# Revit family: FLAKE-PDI100NDFWSxx0DPO0400
name_source: partatom
category: Leuchten
units: mm (PartAtom-declared; Revit-internal decimal feet)

## family parameters
Basisbauteil = Fläche
Beim Laden mit Abzugskörper schneiden = Nein
Bemaßung runder Anschluss = Durchmesser verwenden
Gemeinsam genutzt = Nein
Lichtquelle = Ja
OmniClass-Nummer = 23.80.70.11
OmniClass-Titel = Luminaries for Internal Lighting
Raumberechnungspunkt = Nein
Teiletyp = Normal

## types (2) — shared parameters
Baugruppenkennzeichen = D5020200
Datei für fotometrisches Netz = FLAKE-PDI.IES
Emissionsform beim Rendern sichtbar = Nein
Farbfilter = 16777215
Farbtemperaturverschiebung bei Dämpfen der Lampe = <Keine Auswahl>
Hersteller = RIDI Leuchten GmbH
Lampe = LED
Modell = 0627725AH
Neigungswinkel = 90.00°
Scheinlast = 32 VA
URL = www.ridi.de
Von Breite des Rechtecks ausssenden = 993 mm  [stored 3.25787 ft]
Von Länge des Rechtecks aussenden = 133 mm  [stored 0.436352 ft]
brand = RIDI
conformity mark = CE
electrical safety class = 1
height = 42 mm  [stored 0.137795 ft]
ingress protection (IP) code = IP20
length = 1010 mm  [stored 3.31365 ft]
nominal frequency = 50-60Hz
nominal voltage = 230
rated input power = 32
voltage type (AC, DC, UC) = AC
weight = 4,2
width = 150 mm
zero-valued in all types: Vorgabe-Ansicht

## type names (no varying parameters)
- FLAKE-PDI100NDFWS830DPO0400
- FLAKE-PDI100NDFWS840DPO0400

note: column(s) folded — value = type name in every type: product name

note: [stored X ft] marks values corroborated as IEEE doubles in the binary element streams (Revit-internal decimal feet)
